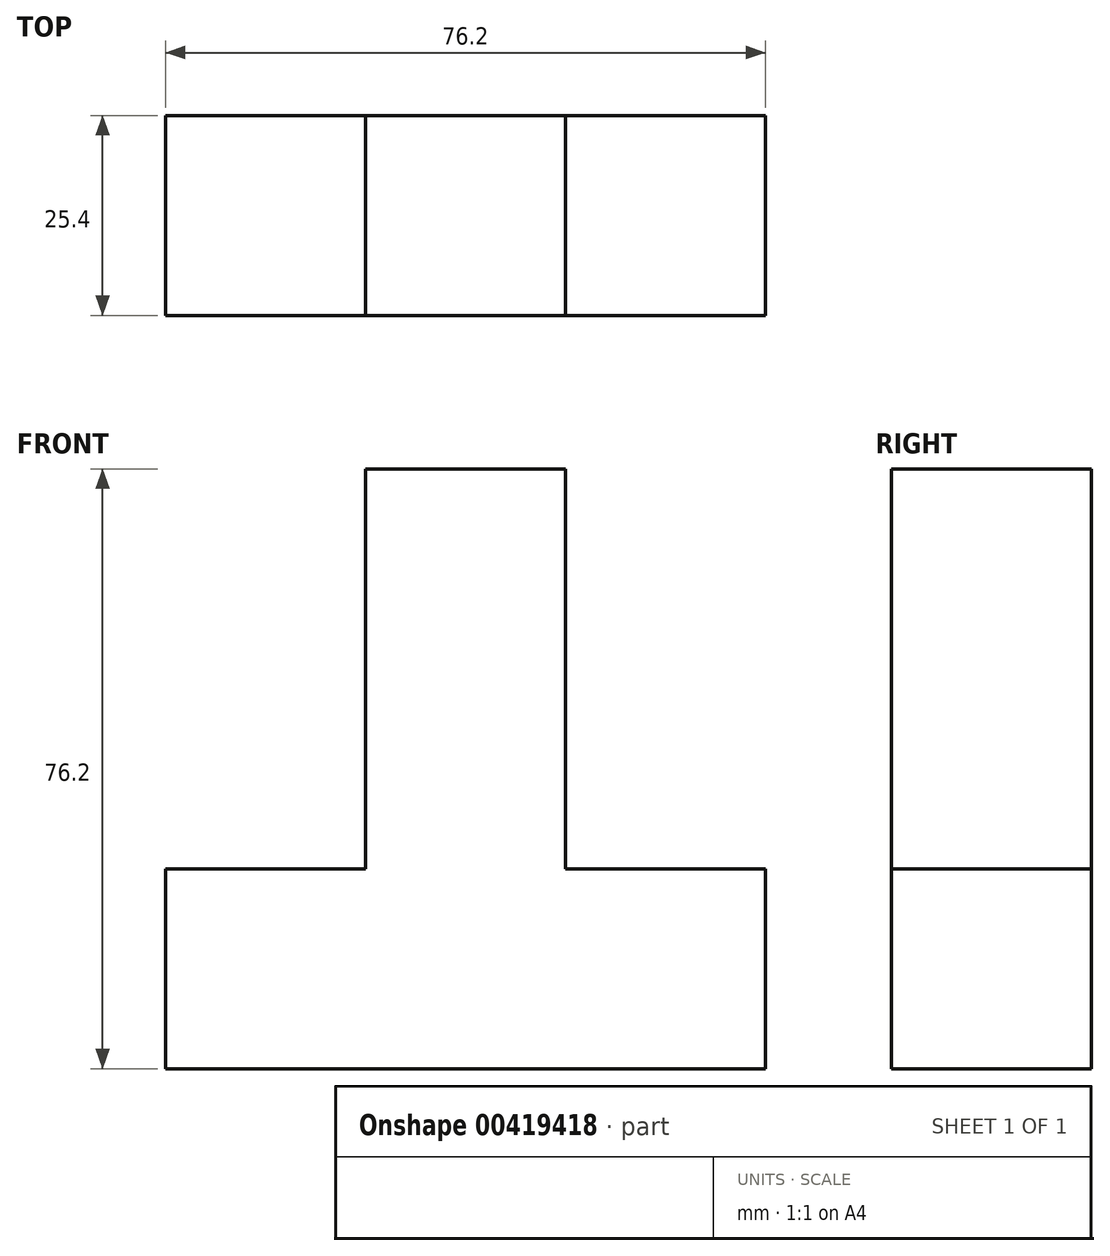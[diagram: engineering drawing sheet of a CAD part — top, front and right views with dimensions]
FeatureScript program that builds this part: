
annotation { "Feature Type Name" : "Feature", "Feature Type Description" : "" }
export const myFeature = defineFeature(function(context is Context, id is Id, definition is map)
    precondition{}
    {
        {
            var Q0;
            Q0=qCreatedBy(makeId("Front.planeOp"),FACE);
            var sketch = newSketch(context, id + "F0", { "sketchPlane" : qUnion([Q0])});
            skLineSegment(sketch, "E0", {"start": v(-21.77, 47.75) * mm, "end": v(-21.77, -3.05) * mm});
            skLineSegment(sketch, "E1", {"start": v(-21.77, 47.75) * mm, "end": v(3.63, 47.75) * mm});
            skLineSegment(sketch, "E2", {"start": v(3.63, 47.75) * mm, "end": v(3.63, -3.05) * mm});
            skLineSegment(sketch, "E3", {"start": v(-21.77, -3.05) * mm, "end": v(-47.17, -3.05) * mm});
            skLineSegment(sketch, "E4", {"start": v(3.63, -3.05) * mm, "end": v(29.03, -3.05) * mm});
            skLineSegment(sketch, "E5", {"start": v(29.03, -3.05) * mm, "end": v(29.03, -28.45) * mm});
            skLineSegment(sketch, "E6", {"start": v(-47.17, -3.05) * mm, "end": v(-47.17, -28.45) * mm});
            skLineSegment(sketch, "E7", {"start": v(29.03, -28.45) * mm, "end": v(-47.17, -28.45) * mm});
            skSolve(sketch);
        }
        {
            var Q0;
            Q0 = qSketchRegion(id + "F0", true);
            extrude(context, id + "F1", {"entities" : qUnion([Q0]), "depth" : 25.4 * mm});
        }
    });
